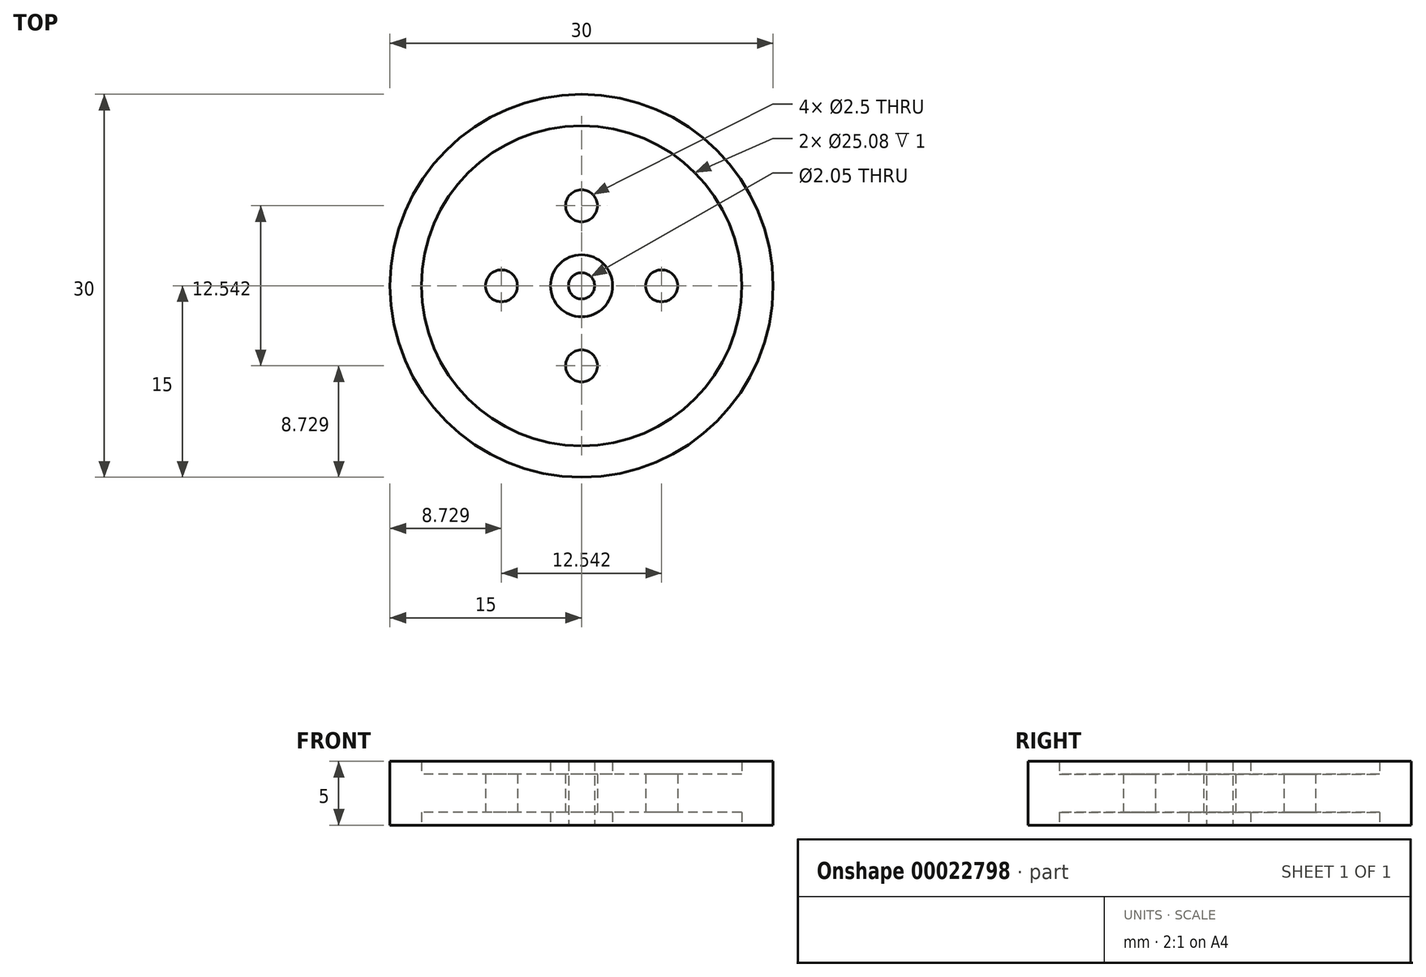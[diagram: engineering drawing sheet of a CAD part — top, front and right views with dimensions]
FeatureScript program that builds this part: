
annotation { "Feature Type Name" : "Feature", "Feature Type Description" : "" }
export const myFeature = defineFeature(function(context is Context, id is Id, definition is map)
    precondition{}
    {
        {
            var Q0;
            Q0=qCreatedBy(makeId("Top.planeOp"),FACE);
            var sketch = newSketch(context, id + "F0", { "sketchPlane" : qUnion([Q0])});
            skCircle(sketch, "E0", {"center": v(0, 0) * mm, "radius": 15 * mm});
            skCircle(sketch, "E1", {"center": v(0, 0) * mm, "radius": 12.54 * mm});
            skPoint(sketch, "E2.orphan", {"position": v(-11.52, 4.96) * mm});
            skCircle(sketch, "E3", {"center": v(0, 0) * mm, "radius": 2.43 * mm});
            skCircle(sketch, "E4", {"center": v(0, 0) * mm, "radius": 1.02 * mm});
            skLineSegment(sketch, "E5", {"start": v(-2.5, 12.29) * mm, "end": v(-2.5, 14.79) * mm});
            skPoint(sketch, "E6.center.orphan", {"position": v(-5.76, 2.48) * mm});
            skLineSegment(sketch, "E7.trimOffspring", {"start": v(-1.02, 0) * mm, "end": v(1.02, 0) * mm});
            skPoint(sketch, "E8.start.orphan", {"position": v(-15, 0) * mm});
            skLineSegment(sketch, "E9", {"start": v(0, 0) * mm, "end": v(0, 12.54) * mm});
            skCircle(sketch, "E10", {"center": v(0, 6.27) * mm, "radius": 1.25 * mm});
            skLineSegment(sketch, "E11", {"start": v(-1.25, 6.24) * mm, "end": v(1.25, 6.24) * mm});
            skCircle(sketch, "E12.1.0", {"center": v(-6.27, 0) * mm, "radius": 1.25 * mm});
            skCircle(sketch, "E12.2.0", {"center": v(0, -6.27) * mm, "radius": 1.25 * mm});
            skCircle(sketch, "E12.3.0", {"center": v(6.27, 0) * mm, "radius": 1.25 * mm});
            skSolve(sketch);
        }
        {
            var Q0;
            Q0=makeQuery(id+"F0.imprint","IMPRINT",FACE,{"disambiguationData":[TD([[makeQuery(id+"F0.imprint","IMPRINT",EDGE,{"derivedFrom":sQuery(id+"F0.wireOp",EDGE,"E0")}),1.0]])]});
            extrude(context, id + "F1", {"entities" : qUnion([Q0]), "endBound" : BoundingType.SYMMETRIC, "depth" : 5 * mm});
        }
        {
            var Q0;
            Q0=qSketchRegion(id+"F0",true);
            var Q1;
            Q1=makeQuery(id+"F0.imprint","IMPRINT",FACE,{"disambiguationData":[TD([[makeQuery(id+"F0.imprint","IMPRINT",EDGE,{"derivedFrom":sQuery(id+"F0.wireOp",EDGE,"E1")}),1.0]])]});
            extrude(context, id + "F2", {"entities" : qUnion([Q0, Q1]), "operationType" : NewBodyOperationType.ADD, "endBound" : BoundingType.SYMMETRIC, "depth" : 3 * mm});
        }
        {
            var Q0;
            Q0=makeQuery(id+"F0.imprint","IMPRINT",FACE,{"disambiguationData":[TD([[makeQuery(id+"F0.imprint","IMPRINT",EDGE,{"derivedFrom":sQuery(id+"F0.wireOp",EDGE,"E3")}),1.0]])]});
            extrude(context, id + "F3", {"entities" : qUnion([Q0]), "operationType" : NewBodyOperationType.ADD, "endBound" : BoundingType.SYMMETRIC, "depth" : 5 * mm});
        }
    });
